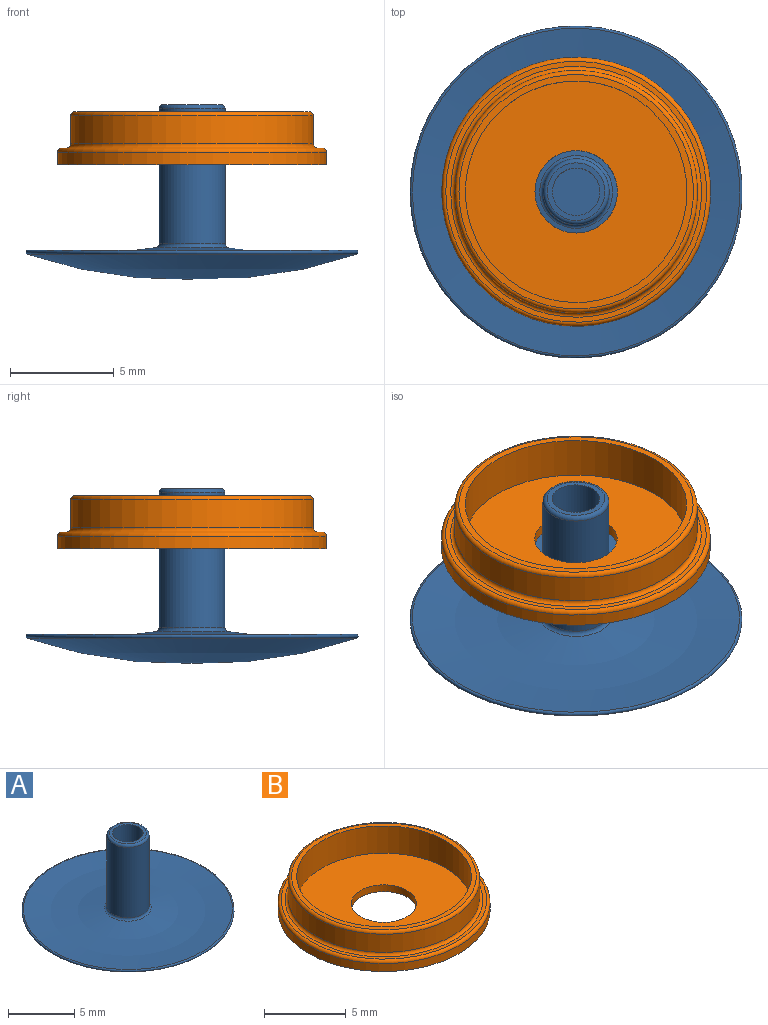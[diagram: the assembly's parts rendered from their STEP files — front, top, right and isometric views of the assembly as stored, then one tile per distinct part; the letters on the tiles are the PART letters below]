
ASSEMBLY  parts=2 mates=2
PART A: 9 faces, bbox 17.3x17.3x8.4 mm
  f0: plane 2.78x2.78mm, normal (0,0,1), area 2mm2, adj f6,f7
  f1: torus R=0.58mm, axis (0,0,-1), area 202.7mm2, adj f2
  f2: torus R=7.9mm, axis (0,0,-1), area 14.6mm2, adj f1,f3
  f3: torus R=5.24mm, axis (0,0,-1), area 186.3mm2, adj f2,f4
  f4: torus R=1.79mm, axis (0,0,-1), area 2.9mm2, adj f3,f5
  f5: cylinder r=1.59mm len=6.49mm, axis (0,0,-1), area 64.8mm2, adj f4,f6
  f6: torus R=1.39mm, axis (0,0,-1), area 3mm2, adj f0,f5
  f7: cylinder r=1.14mm len=6.86mm, axis (0,0,1), area 49.3mm2, adj f0,f8
  f8: plane 2.29x2.29mm, normal (0,0,1), area 4.1mm2, adj f7
PART B: 11 faces, bbox 14x14x2.5 mm
  f0: cylinder r=1.98mm len=3.97mm, axis (0,0,-1), area 6.3mm2, adj f5,f10
  f1: torus R=6.04mm, axis (0,0,-1), area 11.6mm2, adj f2,f8
  f2: cylinder r=5.84mm len=11.68mm, axis (0,0,-1), area 49.5mm2, adj f1,f3
  f3: torus R=5.64mm, axis (0,0,-1), area 11.3mm2, adj f2,f4
  f4: plane 11.29x11.29mm, normal (0,0,1), area 10.7mm2, adj f3,f9
  f5: plane 12.95x12.95mm, normal (0,0,-1), area 119.4mm2, adj f0,f6
  f6: cylinder r=6.48mm len=12.95mm, axis (0,0,-1), area 24.2mm2, adj f5,f7
  f7: torus R=6.28mm, axis (0,0,-1), area 12.5mm2, adj f6,f8
  f8: plane 12.56x12.56mm, normal (0,0,1), area 9.2mm2, adj f1,f7
  f9: cylinder r=5.33mm len=10.67mm, axis (0,0,1), area 68.1mm2, adj f4,f10
  f10: plane 10.67x10.67mm, normal (0,0,1), area 77mm2, adj f0,f9
PLACE A at identity fixed
PLACE B t=(0,0,4.74)mm
MATE slider B.f0 <-> A.f1  axis (0,0,-1) through (0,0,5.24)mm
MATE fastened A.f1 <-> B.f0  axis (0,0,-1) through (0,0,0.44)mm
